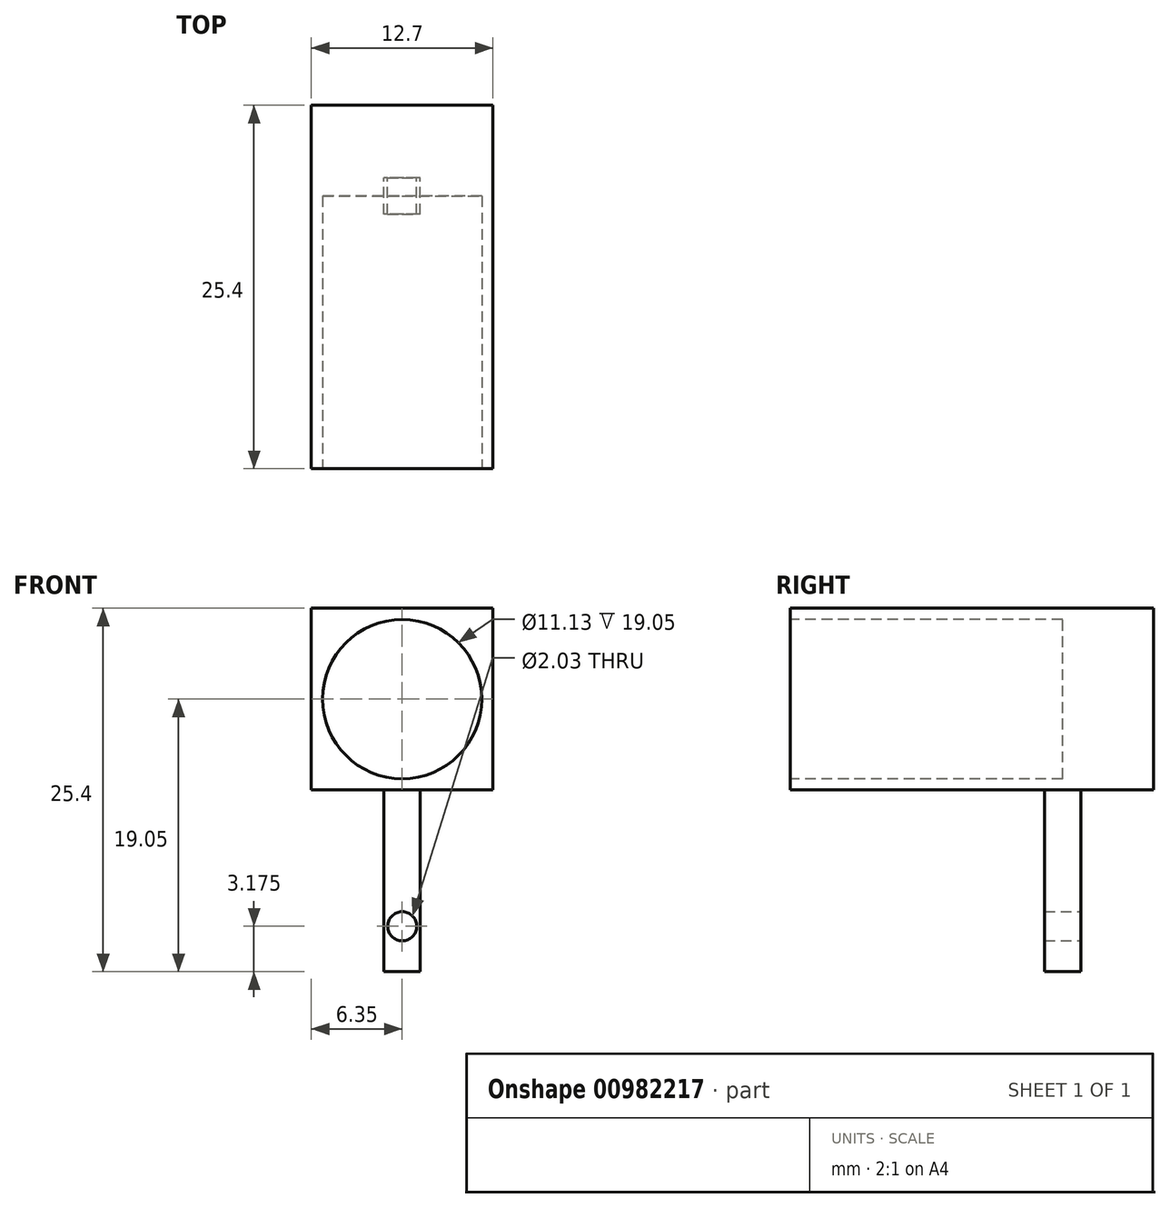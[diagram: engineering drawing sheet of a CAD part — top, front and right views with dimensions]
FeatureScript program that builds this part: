
annotation { "Feature Type Name" : "Feature", "Feature Type Description" : "" }
export const myFeature = defineFeature(function(context is Context, id is Id, definition is map)
    precondition{}
    {
        {
            var Q0;
            Q0=qCreatedBy(makeId("Front.planeOp"),FACE);
            var sketch = newSketch(context, id + "F0", { "sketchPlane" : qUnion([Q0])});
            skLineSegment(sketch, "E0.bottom", {"start": v(6.35, -6.35) * mm, "end": v(-6.35, -6.35) * mm});
            skLineSegment(sketch, "E0.top", {"start": v(6.35, 6.35) * mm, "end": v(-6.35, 6.35) * mm});
            skLineSegment(sketch, "E0.left", {"start": v(6.35, -6.35) * mm, "end": v(6.35, 6.35) * mm});
            skLineSegment(sketch, "E0.right", {"start": v(-6.35, -6.35) * mm, "end": v(-6.35, 6.35) * mm});
            skPoint(sketch, "E0.middle", {"position": v(0, 0) * mm});
            skSolve(sketch);
        }
        {
            var Q0;
            Q0=makeQuery(id+"F0.imprint","IMPRINT",FACE,{"disambiguationData":[TD([[makeQuery(id+"F0.imprint","IMPRINT",EDGE,{"derivedFrom":sQuery(id+"F0.wireOp",EDGE,"E0.bottom")}),-1.0]])]});
            extrude(context, id + "F1", {"entities" : qUnion([Q0]), "oppositeDirection" : true, "depth" : 25.4 * mm, "offsetDistance" : 25.4 * mm});
        }
        {
            var Q0;
            Q0=makeQuery(id+"F1.opExtrude","CAP_FACE",FACE,{"disambiguationData":[OSD([sQuery(id+"F0.wireOp",EDGE,"E0.bottom"),sQuery(id+"F0.wireOp",EDGE,"E0.top"),sQuery(id+"F0.wireOp",EDGE,"E0.left"),sQuery(id+"F0.wireOp",EDGE,"E0.right")])],"isStart":true});
            var sketch = newSketch(context, id + "F2", { "sketchPlane" : qUnion([Q0])});
            skCircle(sketch, "E1", {"center": v(0, 0) * mm, "radius": 5.56 * mm});
            skSolve(sketch);
        }
        {
            var Q0;
            Q0=makeQuery(id+"F2.imprint","IMPRINT",FACE,{"disambiguationData":[TD([[makeQuery(id+"F2.imprint","IMPRINT",EDGE,{"derivedFrom":sQuery(id+"F2.wireOp",EDGE,"E1")}),1.0]])]});
            extrude(context, id + "F3", {"entities" : qUnion([Q0]), "operationType" : NewBodyOperationType.REMOVE, "oppositeDirection" : true, "depth" : 19.05 * mm, "offsetDistance" : 25.4 * mm});
        }
        {
            var Q0;
            Q0=makeQuery(id+"F1.opExtrude","SWEPT_FACE",FACE,{"disambiguationData":[OSD([sQuery(id+"F0.wireOp",EDGE,"E0.bottom")])]});
            var sketch = newSketch(context, id + "F4", { "sketchPlane" : qUnion([Q0])});
            skLineSegment(sketch, "E2", {"start": v(0, 0) * mm, "end": v(0, -25.4) * mm, "construction": true});
            skLineSegment(sketch, "E3", {"start": v(0, -25.4) * mm, "end": v(-6.35, -12.7) * mm, "construction": true});
            skLineSegment(sketch, "E4", {"start": v(-6.35, -12.7) * mm, "end": v(0, 0) * mm, "construction": true});
            skLineSegment(sketch, "E5", {"start": v(0, 0) * mm, "end": v(6.35, -12.7) * mm, "construction": true});
            skLineSegment(sketch, "E6", {"start": v(6.35, -12.7) * mm, "end": v(0, -25.4) * mm, "construction": true});
            skLineSegment(sketch, "E7", {"start": v(-6.35, -25.4) * mm, "end": v(6.35, 0) * mm, "construction": true});
            skLineSegment(sketch, "E8", {"start": v(6.35, 0) * mm, "end": v(-6.35, 0) * mm, "construction": true});
            skLineSegment(sketch, "E9", {"start": v(-6.35, 0) * mm, "end": v(6.35, -25.4) * mm, "construction": true});
            skLineSegment(sketch, "E10", {"start": v(-3.18, -19.05) * mm, "end": v(3.17, -19.05) * mm, "construction": true});
            skPoint(sketch, "E11", {"position": v(0, -19.05) * mm});
            skLineSegment(sketch, "E12.bottom", {"start": v(1.27, -17.78) * mm, "end": v(-1.27, -17.78) * mm});
            skLineSegment(sketch, "E12.top", {"start": v(1.27, -20.32) * mm, "end": v(-1.27, -20.32) * mm});
            skLineSegment(sketch, "E12.left", {"start": v(1.27, -17.78) * mm, "end": v(1.27, -20.32) * mm});
            skLineSegment(sketch, "E12.right", {"start": v(-1.27, -17.78) * mm, "end": v(-1.27, -20.32) * mm});
            skSolve(sketch);
        }
        {
            var Q0;
            Q0=makeQuery(id+"F4.imprint","IMPRINT",FACE,{"disambiguationData":[TD([[makeQuery(id+"F4.imprint","IMPRINT",EDGE,{"derivedFrom":sQuery(id+"F4.wireOp",EDGE,"E12.bottom")}),1.0]])]});
            extrude(context, id + "F5", {"entities" : qUnion([Q0]), "operationType" : NewBodyOperationType.ADD, "depth" : 12.7 * mm, "offsetDistance" : 25.4 * mm});
        }
        {
            var Q0;
            Q0=makeQuery(id+"F5.opExtrude","SWEPT_FACE",FACE,{"disambiguationData":[OSD([sQuery(id+"F4.wireOp",EDGE,"E12.top")])]});
            var sketch = newSketch(context, id + "F6", { "sketchPlane" : qUnion([Q0])});
            skLineSegment(sketch, "E13", {"start": v(1.27, -12.7) * mm, "end": v(-1.27, -12.7) * mm, "construction": true});
            skLineSegment(sketch, "E14", {"start": v(-1.27, -12.7) * mm, "end": v(1.27, -19.05) * mm, "construction": true});
            skLineSegment(sketch, "E15", {"start": v(1.27, -12.7) * mm, "end": v(-1.27, -19.05) * mm, "construction": true});
            skCircle(sketch, "E16", {"center": v(0, -15.88) * mm, "radius": 1.02 * mm});
            skSolve(sketch);
        }
        {
            var Q0;
            Q0=makeQuery(id+"F6.imprint","IMPRINT",FACE,{"disambiguationData":[TD([[makeQuery(id+"F6.imprint","IMPRINT",EDGE,{"derivedFrom":sQuery(id+"F6.wireOp",EDGE,"E16")}),1.0]])]});
            extrude(context, id + "F7", {"entities" : qUnion([Q0]), "operationType" : NewBodyOperationType.REMOVE, "oppositeDirection" : true, "depth" : 25.4 * mm, "offsetDistance" : 25.4 * mm});
        }
    });
